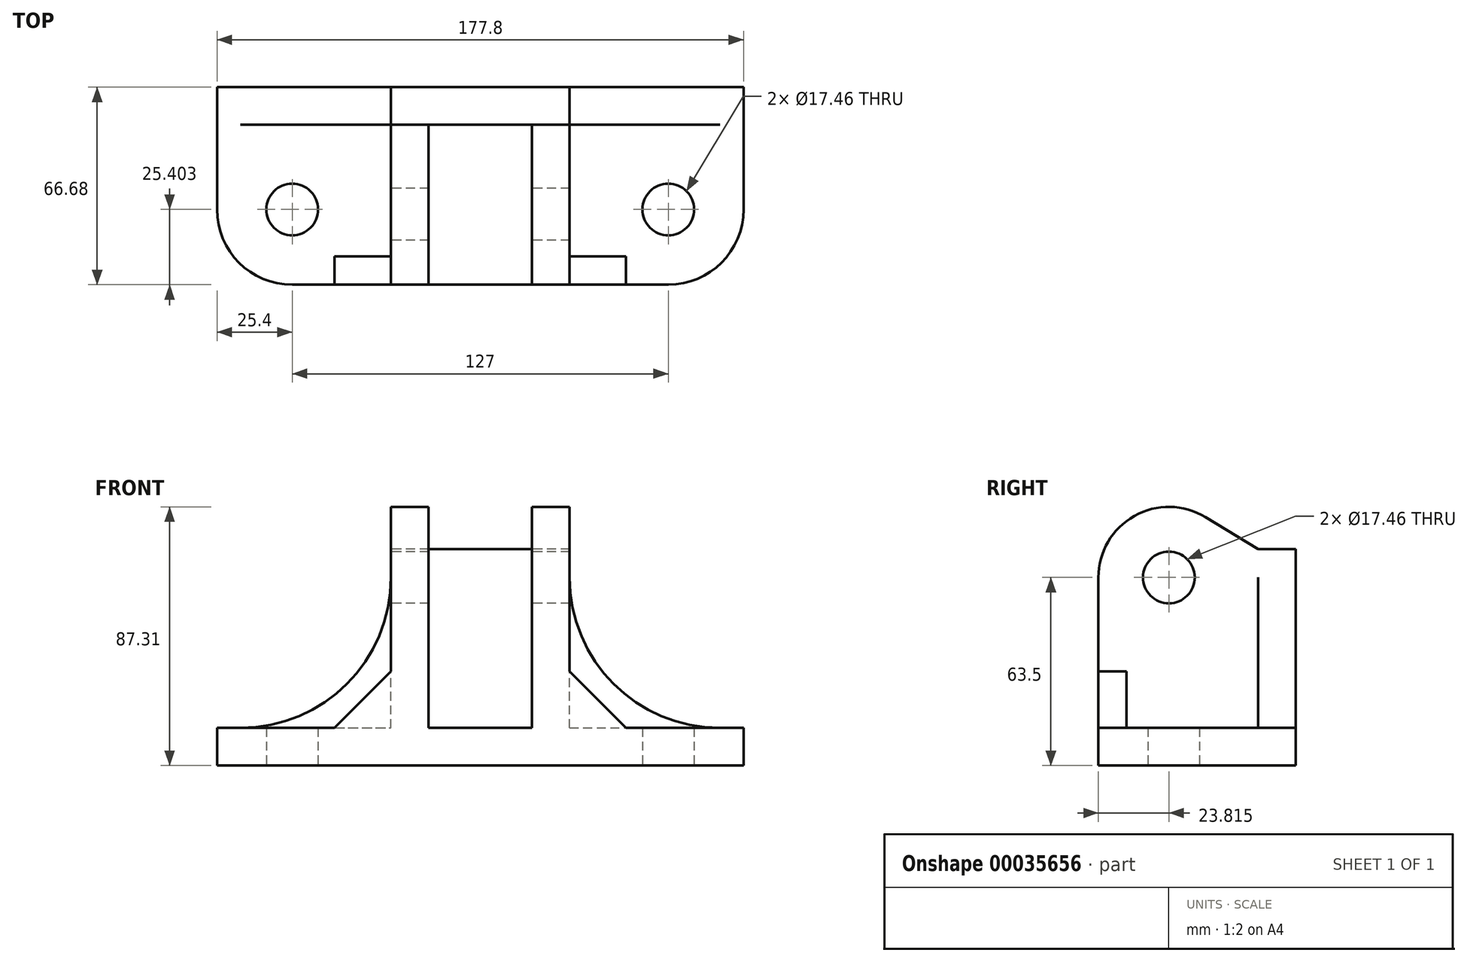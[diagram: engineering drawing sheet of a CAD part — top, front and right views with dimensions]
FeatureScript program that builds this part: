
annotation { "Feature Type Name" : "Feature", "Feature Type Description" : "" }
export const myFeature = defineFeature(function(context is Context, id is Id, definition is map)
    precondition{}
    {
        {
            var Q0;
            Q0=qCreatedBy(makeId("Top.planeOp"),FACE);
            var sketch = newSketch(context, id + "F0", { "sketchPlane" : qUnion([Q0])});
            skLineSegment(sketch, "E0.rect.bottom", {"start": v(-88.9, -33.34) * mm, "end": v(88.9, -33.34) * mm});
            skLineSegment(sketch, "E0.rect.top", {"start": v(-88.9, 33.34) * mm, "end": v(88.9, 33.34) * mm});
            skLineSegment(sketch, "E0.rect.left", {"start": v(-88.9, -33.34) * mm, "end": v(-88.9, 33.34) * mm});
            skLineSegment(sketch, "E0.rect.right", {"start": v(88.9, -33.34) * mm, "end": v(88.9, 33.34) * mm});
            skPoint(sketch, "E0.rect.middle", {"position": v(0, 0) * mm});
            skCircle(sketch, "E1", {"center": v(-63.5, -7.94) * mm, "radius": 8.73 * mm});
            skCircle(sketch, "E2", {"center": v(63.5, -7.94) * mm, "radius": 8.73 * mm});
            skLineSegment(sketch, "E3", {"start": v(0, 33.34) * mm, "end": v(0, -33.34) * mm, "construction": true});
            skCircle(sketch, "E4", {"center": v(-63.5, -7.94) * mm, "radius": 25.4 * mm});
            skCircle(sketch, "E5", {"center": v(63.5, -7.94) * mm, "radius": 25.4 * mm});
            skSolve(sketch);
        }
        {
            var Q0;
            Q0=makeQuery(id+"F0.imprint","IMPRINT",FACE,{"disambiguationData":[TD([[makeQuery(id+"F0.imprint","IMPRINT",EDGE,{"derivedFrom":sQuery(id+"F0.wireOp",EDGE,"E1")}),-1.0]])]});
            var Q1;
            {var subQ8=sQuery(id+"F0.wireOp",EDGE,"E0.rect.top");Q1=makeQuery(id+"F0.imprint","IMPRINT",FACE,{"disambiguationData":[TD([[makeQuery(id+"F0.imprint","IMPRINT",EDGE,{"derivedFrom":subQ8}),-1.0]])]});}
            var Q2;
            Q2=makeQuery(id+"F0.imprint","IMPRINT",FACE,{"disambiguationData":[TD([[makeQuery(id+"F0.imprint","IMPRINT",EDGE,{"derivedFrom":sQuery(id+"F0.wireOp",EDGE,"E2")}),-1.0]])]});
            extrude(context, id + "F1", {"entities" : qUnion([Q0, Q1, Q2]), "depth" : 12.7 * mm});
        }
        {
            var Q0;
            Q0=qCreatedBy(makeId("Right.planeOp"),FACE);
            var sketch = newSketch(context, id + "F2", { "sketchPlane" : qUnion([Q0])});
            skLineSegment(sketch, "E6.0", {"start": v(-33.34, 12.7) * mm, "end": v(-7.94, 12.7) * mm});
            skLineSegment(sketch, "E7.0", {"start": v(-7.94, 12.7) * mm, "end": v(33.34, 12.7) * mm});
            skLineSegment(sketch, "E8", {"start": v(33.34, 12.7) * mm, "end": v(33.34, 73.03) * mm});
            skLineSegment(sketch, "E9", {"start": v(33.34, 73.03) * mm, "end": v(20.64, 73.03) * mm});
            skLineSegment(sketch, "E10", {"start": v(-33.34, 12.7) * mm, "end": v(-33.34, 63.5) * mm});
            skCircle(sketch, "E11", {"center": v(-9.52, 63.5) * mm, "radius": 23.81 * mm});
            skCircle(sketch, "E12", {"center": v(-9.52, 63.5) * mm, "radius": 8.73 * mm});
            skLineSegment(sketch, "E13", {"start": v(20.64, 73.03) * mm, "end": v(0, 85.58) * mm});
            skSolve(sketch);
        }
        {
            var Q0;
            Q0=makeQuery(id+"F2.imprint","IMPRINT",FACE,{"disambiguationData":[TD([[makeQuery(id+"F2.imprint","IMPRINT",EDGE,{"derivedFrom":sQuery(id+"F2.wireOp",EDGE,"E6.0")}),1.0]])]});
            var Q1;
            Q1=makeQuery(id+"F2.imprint","IMPRINT",FACE,{"disambiguationData":[TD([[makeQuery(id+"F2.imprint","IMPRINT",EDGE,{"derivedFrom":sQuery(id+"F2.wireOp",EDGE,"E12")}),-1.0]])]});
            extrude(context, id + "F3", {"entities" : qUnion([Q0, Q1]), "operationType" : NewBodyOperationType.ADD, "endBound" : BoundingType.SYMMETRIC, "depth" : 60.32 * mm});
        }
        {
            var Q0;
            Q0=qCreatedBy(makeId("Right.planeOp"),FACE);
            var sketch = newSketch(context, id + "F4", { "sketchPlane" : qUnion([Q0])});
            skLineSegment(sketch, "E14.0", {"start": v(33.34, 73.03) * mm, "end": v(20.64, 73.03) * mm});
            skLineSegment(sketch, "E15.0", {"start": v(-7.94, 12.7) * mm, "end": v(33.34, 12.7) * mm});
            skLineSegment(sketch, "E16", {"start": v(20.64, 73.03) * mm, "end": v(20.64, 12.7) * mm});
            skArc(sketch, "E17.0", {"start": v(2.85, 83.84) * mm, "mid": v(-21.2, 84.26) * mm, "end": v(-33.34, 63.5) * mm});
            skLineSegment(sketch, "E18.0", {"start": v(20.64, 73.03) * mm, "end": v(2.85, 83.84) * mm});
            skLineSegment(sketch, "E19.0", {"start": v(-33.34, 12.7) * mm, "end": v(-33.34, 63.5) * mm});
            skLineSegment(sketch, "E20.0", {"start": v(-33.34, 12.7) * mm, "end": v(-7.94, 12.7) * mm});
            skSolve(sketch);
        }
        {
            var Q0;
            Q0 = qSketchRegion(id + "F4", true);
            extrude(context, id + "F5", {"entities" : qUnion([Q0]), "operationType" : NewBodyOperationType.REMOVE, "endBound" : BoundingType.SYMMETRIC, "oppositeDirection" : true, "depth" : 34.92 * mm});
        }
        {
            var Q0;
            Q0=makeQuery(id+"F3.boolean.opBoolean","MERGE",FACE,{"derivedFrom":[makeQuery(id+"F1.opExtrude","SWEPT_FACE",FACE,{"disambiguationData":[OSD([sQuery(id+"F0.wireOp",EDGE,"E0.rect.bottom")])]}),makeQuery(id+"F3.opExtrude","SWEPT_FACE",FACE,{"disambiguationData":[OSD([sQuery(id+"F2.wireOp",EDGE,"E10")])]})]});
            var sketch = newSketch(context, id + "F6", { "sketchPlane" : qUnion([Q0])});
            skLineSegment(sketch, "E21.0", {"start": v(30.16, 12.7) * mm, "end": v(30.16, 63.5) * mm});
            skLineSegment(sketch, "E22.0", {"start": v(30.16, 12.7) * mm, "end": v(63.5, 12.7) * mm});
            skLineSegment(sketch, "E23.0", {"start": v(-30.16, 12.7) * mm, "end": v(-30.16, 63.5) * mm});
            skLineSegment(sketch, "E24.0", {"start": v(-63.5, 12.7) * mm, "end": v(-30.16, 12.7) * mm});
            skLineSegment(sketch, "E25", {"start": v(30.16, 31.75) * mm, "end": v(49.21, 12.7) * mm});
            skLineSegment(sketch, "E26", {"start": v(-30.16, 31.75) * mm, "end": v(-49.21, 12.7) * mm});
            skSolve(sketch);
        }
        {
            var Q0;
            {var subQ0=sQuery(id+"F6.wireOp",EDGE,"E26");Q0=makeQuery(id+"F6.imprint","IMPRINT",FACE,{"disambiguationData":[TD([[makeQuery(id+"F6.imprint","IMPRINT",EDGE,{"derivedFrom":subQ0}),1.0]])]});}
            var Q1;
            {var subQ0=sQuery(id+"F6.wireOp",EDGE,"E25");Q1=makeQuery(id+"F6.imprint","IMPRINT",FACE,{"disambiguationData":[TD([[makeQuery(id+"F6.imprint","IMPRINT",EDGE,{"derivedFrom":subQ0}),-1.0]])]});}
            extrude(context, id + "F7", {"entities" : qUnion([Q0, Q1]), "operationType" : NewBodyOperationType.ADD, "oppositeDirection" : true, "depth" : 9.52 * mm});
        }
        {
            var Q0;
            Q0=makeQuery(id+"F3.boolean.opBoolean","MERGE",FACE,{"derivedFrom":[makeQuery(id+"F1.opExtrude","SWEPT_FACE",FACE,{"disambiguationData":[OSD([sQuery(id+"F0.wireOp",EDGE,"E0.rect.top")])]}),makeQuery(id+"F3.opExtrude","SWEPT_FACE",FACE,{"disambiguationData":[OSD([sQuery(id+"F2.wireOp",EDGE,"E8")])]})]});
            var sketch = newSketch(context, id + "F8", { "sketchPlane" : qUnion([Q0])});
            skLineSegment(sketch, "E27.0", {"start": v(-80.96, 12.7) * mm, "end": v(-88.9, 12.7) * mm});
            skLineSegment(sketch, "E28.0", {"start": v(-30.16, 63.5) * mm, "end": v(-30.16, 73.03) * mm});
            skLineSegment(sketch, "E29.0", {"start": v(30.16, 63.5) * mm, "end": v(30.16, 73.03) * mm});
            skLineSegment(sketch, "E30.0", {"start": v(88.9, 12.7) * mm, "end": v(80.96, 12.7) * mm});
            skPoint(sketch, "E31.visualSharp", {"position": v(-30.16, 12.7) * mm});
            skArc(sketch, "E31.filletArc", {"start": v(-80.96, 12.7) * mm, "mid": v(-45.04, 27.58) * mm, "end": v(-30.16, 63.5) * mm});
            skPoint(sketch, "E32.visualSharp", {"position": v(30.16, 12.7) * mm});
            skArc(sketch, "E32.filletArc", {"start": v(30.16, 63.5) * mm, "mid": v(45.04, 27.58) * mm, "end": v(80.96, 12.7) * mm});
            skSolve(sketch);
        }
        {
            var Q0;
            {var subQ4=sQuery(id+"F8.wireOp",EDGE,"E31.filletArc");Q0=makeQuery(id+"F8.imprint","IMPRINT",FACE,{"disambiguationData":[TD([[makeQuery(id+"F8.imprint","IMPRINT",EDGE,{"derivedFrom":subQ4}),-1.0]])]});}
            var Q1;
            {var subQ4=sQuery(id+"F8.wireOp",EDGE,"E32.filletArc");Q1=makeQuery(id+"F8.imprint","IMPRINT",FACE,{"disambiguationData":[TD([[makeQuery(id+"F8.imprint","IMPRINT",EDGE,{"derivedFrom":subQ4}),-1.0]])]});}
            var Q2;
            Q2=makeQuery(id+"F5.boolean.opBoolean","COPY",FACE,{"derivedFrom":makeQuery(id+"F5.opExtrude","SWEPT_FACE",FACE,{"disambiguationData":[OSD([sQuery(id+"F4.wireOp",EDGE,"E16")])]})});
            extrude(context, id + "F9", {"entities" : qUnion([Q0, Q1]), "operationType" : NewBodyOperationType.ADD, "endBound" : BoundingType.UP_TO_SURFACE, "oppositeDirection" : true, "endBoundEntityFace" : qUnion([Q2]), "depth" : 25.4 * mm});
        }
    });
